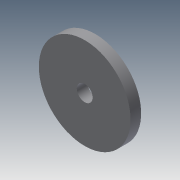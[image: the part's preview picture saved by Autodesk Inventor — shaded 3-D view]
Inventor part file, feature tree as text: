
AUTODESK INVENTOR PART (.ipt)
format: ipt  version: 2013 (Build 170138000, 138)  size: 75,264 bytes
history: native  units: mm
features: sketch x2, extrude x2
ambient origin geometry x8: Origin, YZ Plane, XZ Plane, XY Plane, X Axis, Y Axis, Z Axis, Center Point
bodies: Solid1 (feature_tree)
feature tree (4):
  sketch  "Sketch1"  dims[d0=34.65mm d1=6.0mm]
  sketch  "Sketch2"  dims[d2=4.0mm d3=0.0mm d4=4.0mm d5=0.0mm]
  extrude  "Extrusion1"  Depth=6.0mm
  extrude  "Extrusion2"  Depth=4.0mm TaperAngle=0.0deg
